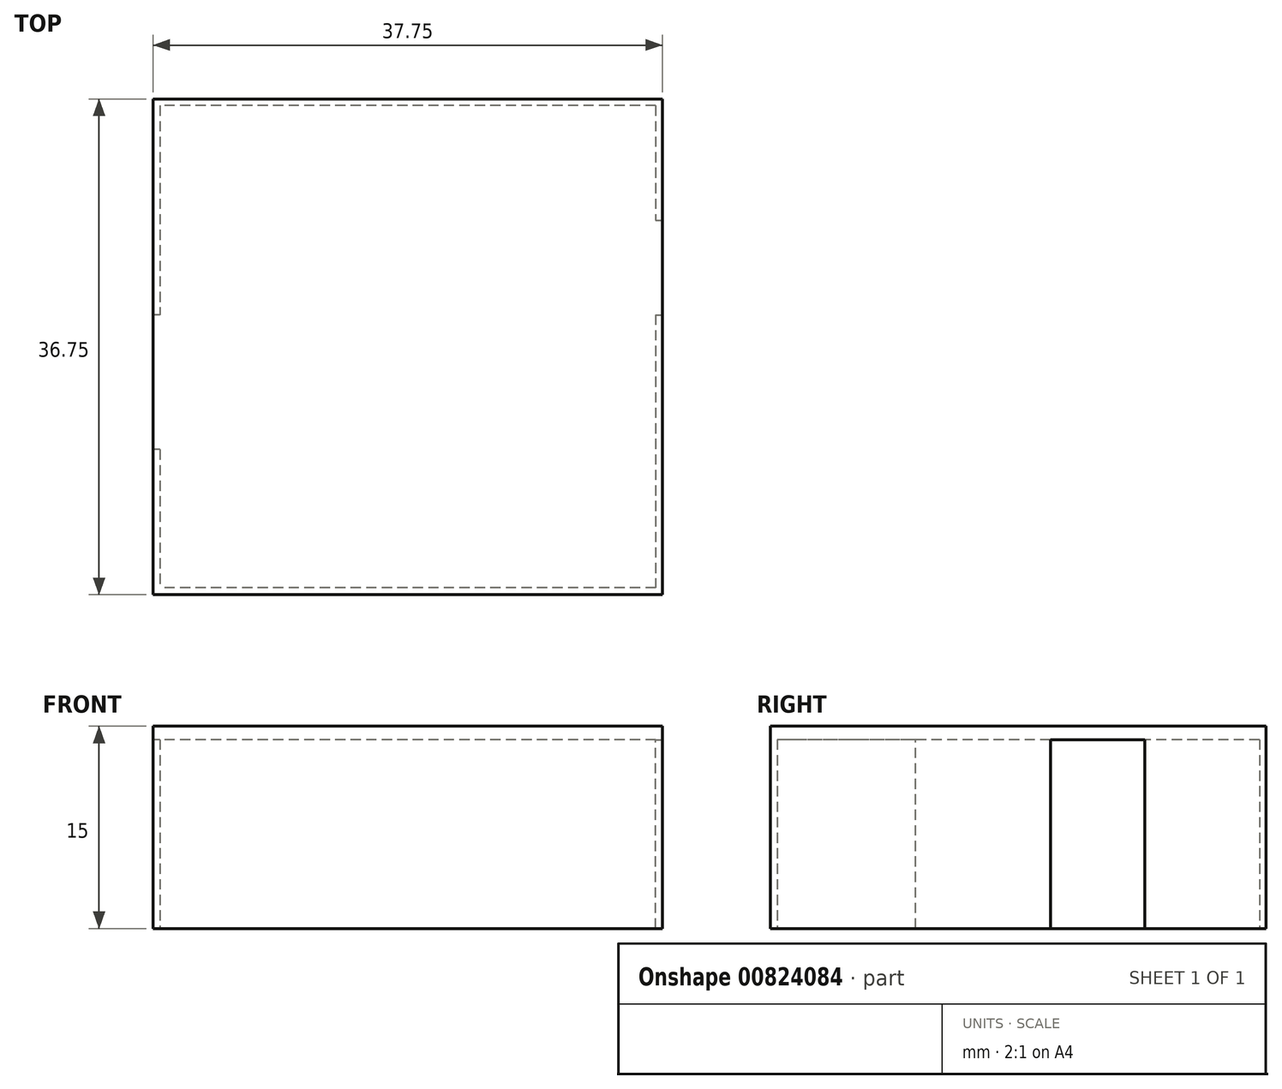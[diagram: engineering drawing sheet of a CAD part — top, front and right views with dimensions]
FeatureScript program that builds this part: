
annotation { "Feature Type Name" : "Feature", "Feature Type Description" : "" }
export const myFeature = defineFeature(function(context is Context, id is Id, definition is map)
    precondition{}
    {
        {
            var Q0;
            Q0=qCreatedBy(makeId("Top.planeOp"),FACE);
            var sketch = newSketch(context, id + "F0", { "sketchPlane" : qUnion([Q0])});
            skLineSegment(sketch, "E0.bottom", {"start": v(-10.24, 23.88) * mm, "end": v(27.51, 23.88) * mm});
            skLineSegment(sketch, "E0.top", {"start": v(-10.24, -12.87) * mm, "end": v(27.51, -12.87) * mm});
            skLineSegment(sketch, "E0.left", {"start": v(-10.24, 23.88) * mm, "end": v(-10.24, -12.87) * mm});
            skLineSegment(sketch, "E0.right", {"start": v(27.51, 23.88) * mm, "end": v(27.51, -12.87) * mm});
            skSolve(sketch);
        }
        {
            var Q0;
            Q0=makeQuery(id+"F0.imprint","IMPRINT",FACE,{"disambiguationData":[TD([[makeQuery(id+"F0.imprint","IMPRINT",EDGE,{"derivedFrom":sQuery(id+"F0.wireOp",EDGE,"E0.bottom")}),-1.0]])]});
            extrude(context, id + "F1", {"entities" : qUnion([Q0]), "depth" : 15 * mm, "offsetDistance" : 25 * mm});
        }
        {
            var Q0;
            Q0=makeQuery(id+"F1.opExtrude","CAP_FACE",FACE,{"disambiguationData":[OSD([sQuery(id+"F0.wireOp",EDGE,"E0.bottom"),sQuery(id+"F0.wireOp",EDGE,"E0.top"),sQuery(id+"F0.wireOp",EDGE,"E0.left"),sQuery(id+"F0.wireOp",EDGE,"E0.right")])],"isStart":true});
            var sketch = newSketch(context, id + "F2", { "sketchPlane" : qUnion([Q0])});
            skLineSegment(sketch, "E1.bottom", {"start": v(27.01, -23.38) * mm, "end": v(-9.74, -23.38) * mm});
            skLineSegment(sketch, "E1.top", {"start": v(27.01, 12.37) * mm, "end": v(-9.74, 12.37) * mm});
            skLineSegment(sketch, "E1.left", {"start": v(27.01, -23.38) * mm, "end": v(27.01, 5.68) * mm});
            skLineSegment(sketch, "E1.right", {"start": v(-9.74, -23.38) * mm, "end": v(-9.74, -14.32) * mm});
            skLineSegment(sketch, "E2.left", {"start": v(27.01, 8.97) * mm, "end": v(27.01, 5.68) * mm});
            skLineSegment(sketch, "E3.left", {"start": v(-9.74, -14.32) * mm, "end": v(-9.74, -10.73) * mm});
            skLineSegment(sketch, "E4.trimOffspring", {"start": v(27.01, 8.97) * mm, "end": v(27.01, 12.37) * mm});
            skLineSegment(sketch, "E5.trimOffspring", {"start": v(-9.74, -10.73) * mm, "end": v(-9.74, 12.37) * mm});
            skSolve(sketch);
        }
        {
            var Q0;
            Q0=makeQuery(id+"F2.imprint","IMPRINT",FACE,{"disambiguationData":[TD([[makeQuery(id+"F2.imprint","IMPRINT",EDGE,{"derivedFrom":sQuery(id+"F2.wireOp",EDGE,"E1.bottom")}),-1.0]])]});
            extrude(context, id + "F3", {"entities" : qUnion([Q0]), "operationType" : NewBodyOperationType.REMOVE, "oppositeDirection" : true, "depth" : 14 * mm, "offsetDistance" : 25 * mm});
        }
        {
            var Q0;
            Q0=makeQuery(id+"F1.opExtrude","SWEPT_FACE",FACE,{"disambiguationData":[OSD([sQuery(id+"F0.wireOp",EDGE,"E0.right")])]});
            var sketch = newSketch(context, id + "F4", { "sketchPlane" : qUnion([Q0])});
            skLineSegment(sketch, "E6.bottom", {"start": v(7.88, 0) * mm, "end": v(14.88, 0) * mm});
            skLineSegment(sketch, "E6.top", {"start": v(7.88, 14) * mm, "end": v(14.88, 14) * mm});
            skLineSegment(sketch, "E6.left", {"start": v(7.88, 0) * mm, "end": v(7.88, 14) * mm});
            skLineSegment(sketch, "E6.right", {"start": v(14.88, 0) * mm, "end": v(14.88, 14) * mm});
            skSolve(sketch);
        }
        {
            var Q0;
            Q0=makeQuery(id+"F4.imprint","IMPRINT",FACE,{"disambiguationData":[TD([[makeQuery(id+"F4.imprint","IMPRINT",EDGE,{"derivedFrom":sQuery(id+"F4.wireOp",EDGE,"E6.bottom")}),-1.0]])]});
            extrude(context, id + "F5", {"entities" : qUnion([Q0]), "operationType" : NewBodyOperationType.REMOVE, "oppositeDirection" : true, "depth" : 5 * mm, "offsetDistance" : 25 * mm});
        }
        {
            var Q0;
            Q0=makeQuery(id+"F1.opExtrude","SWEPT_FACE",FACE,{"disambiguationData":[OSD([sQuery(id+"F0.wireOp",EDGE,"E0.left")])]});
            var sketch = newSketch(context, id + "F6", { "sketchPlane" : qUnion([Q0])});
            skLineSegment(sketch, "E7.bottom", {"start": v(-7.88, 0) * mm, "end": v(2.12, 0) * mm});
            skLineSegment(sketch, "E7.top", {"start": v(-7.88, 14) * mm, "end": v(2.12, 14) * mm});
            skLineSegment(sketch, "E7.left", {"start": v(-7.88, 0) * mm, "end": v(-7.88, 14) * mm});
            skLineSegment(sketch, "E7.right", {"start": v(2.12, 0) * mm, "end": v(2.12, 14) * mm});
            skSolve(sketch);
        }
        {
            var Q0;
            Q0=makeQuery(id+"F6.imprint","IMPRINT",FACE,{"disambiguationData":[TD([[makeQuery(id+"F6.imprint","IMPRINT",EDGE,{"derivedFrom":sQuery(id+"F6.wireOp",EDGE,"E7.bottom")}),1.0]])]});
            extrude(context, id + "F7", {"entities" : qUnion([Q0]), "operationType" : NewBodyOperationType.REMOVE, "oppositeDirection" : true, "depth" : 3 * mm, "offsetDistance" : 25 * mm});
        }
    });
